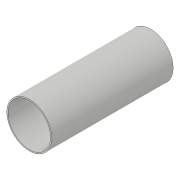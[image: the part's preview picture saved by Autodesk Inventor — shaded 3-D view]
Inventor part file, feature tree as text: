
AUTODESK INVENTOR PART (.ipt)
format: ipt  version: 2019 (Build 230136000, 136)  size: 83,456 bytes
history: native  units: in
note: dims shown in document units (in); Inventor stores cm internally (conversion verified against a paired STEP export)
features: sketch x3, extrude x2
ambient origin geometry x8: Origin, YZ Plane, XZ Plane, XY Plane, X Axis, Y Axis, Z Axis, Center Point
bodies: Solid1 (feature_tree)
feature tree (5):
  sketch  "Sketch1"  dims[d0=1.4567in d1=3.937in d2=0.0in]
  extrude  "Extrusion1"  Depth=3.937in TaperAngle=0.0deg
  extrude  "Extrusion2"  Depth=3.937in TaperAngle=0.0deg
  sketch  "Sketch2"  dims[d3=1.378in d4=3.937in d5=0.0in]
  sketch  "Sketch3"
